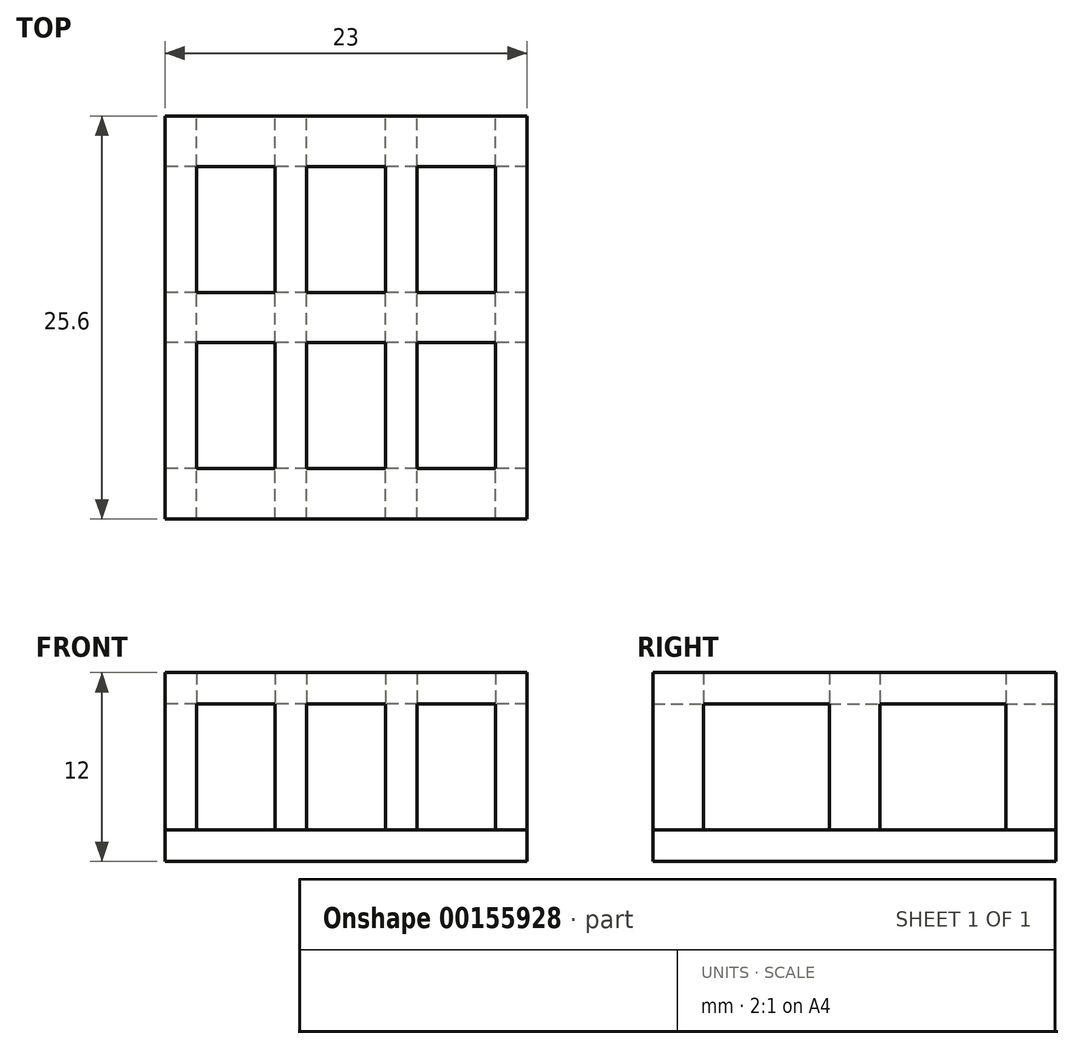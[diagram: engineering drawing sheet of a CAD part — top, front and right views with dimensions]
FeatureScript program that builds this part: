
annotation { "Feature Type Name" : "Feature", "Feature Type Description" : "" }
export const myFeature = defineFeature(function(context is Context, id is Id, definition is map)
    precondition{}
    {
        {
            var Q0;
            Q0=qCreatedBy(makeId("Top.planeOp"),FACE);
            var sketch = newSketch(context, id + "F0", { "sketchPlane" : qUnion([Q0])});
            skLineSegment(sketch, "E0", {"start": v(-38.8, 39.2) * mm, "end": v(-38.8, 40.8) * mm});
            skLineSegment(sketch, "E1", {"start": v(-33.8, 39.2) * mm, "end": v(-33.8, 40.8) * mm});
            skLineSegment(sketch, "E2", {"start": v(-31.8, 39.2) * mm, "end": v(-31.8, 40.8) * mm});
            skLineSegment(sketch, "E3", {"start": v(-26.8, 39.2) * mm, "end": v(-26.8, 40.8) * mm});
            skLineSegment(sketch, "E4", {"start": v(-24.8, 39.2) * mm, "end": v(-24.8, 40.8) * mm});
            skLineSegment(sketch, "E5", {"start": v(-19.8, 39.2) * mm, "end": v(-19.8, 40.8) * mm});
            skLineSegment(sketch, "E6", {"start": v(-17.8, 39.2) * mm, "end": v(-17.8, 40.8) * mm});
            skLineSegment(sketch, "E7.trimOffspring", {"start": v(-17.8, 40.8) * mm, "end": v(-40.8, 40.8) * mm});
            skLineSegment(sketch, "E8.trimOffspring", {"start": v(-17.8, 37.6) * mm, "end": v(-40.8, 37.6) * mm});
            skLineSegment(sketch, "E9.trimOffspring", {"start": v(-17.8, 29.6) * mm, "end": v(-40.8, 29.6) * mm});
            skLineSegment(sketch, "E10.trimOffspring", {"start": v(-17.8, 26.4) * mm, "end": v(-40.8, 26.4) * mm});
            skLineSegment(sketch, "E11.trimOffspring", {"start": v(-17.8, 18.4) * mm, "end": v(-40.8, 18.4) * mm});
            skLineSegment(sketch, "E12.trimOffspring", {"start": v(-17.8, 15.2) * mm, "end": v(-40.8, 15.2) * mm});
            skPoint(sketch, "E13.orphan", {"position": v(40.8, -40.8) * mm});
            skPoint(sketch, "E14.left.end.orphan", {"position": v(40.8, 40.8) * mm});
            skLineSegment(sketch, "E15.trimOffspring", {"start": v(-17.8, 15.2) * mm, "end": v(-17.8, 39.2) * mm});
            skLineSegment(sketch, "E16.trimOffspring", {"start": v(-19.8, 15.2) * mm, "end": v(-19.8, 39.2) * mm});
            skLineSegment(sketch, "E17.trimOffspring", {"start": v(-24.8, 15.2) * mm, "end": v(-24.8, 39.2) * mm});
            skLineSegment(sketch, "E18.trimOffspring", {"start": v(-26.8, 15.2) * mm, "end": v(-26.8, 39.2) * mm});
            skLineSegment(sketch, "E19.trimOffspring", {"start": v(-31.8, 15.2) * mm, "end": v(-31.8, 39.2) * mm});
            skLineSegment(sketch, "E20.trimOffspring", {"start": v(-33.8, 15.2) * mm, "end": v(-33.8, 39.2) * mm});
            skLineSegment(sketch, "E21.trimOffspring", {"start": v(-38.8, 15.2) * mm, "end": v(-38.8, 39.2) * mm});
            skLineSegment(sketch, "E22.trimOffspring", {"start": v(-40.8, 15.2) * mm, "end": v(-40.8, 40.8) * mm});
            skPoint(sketch, "E23.orphan", {"position": v(-4, 37.6) * mm});
            skPoint(sketch, "E24.orphan", {"position": v(-4, 29.6) * mm});
            skSolve(sketch);
        }
        {
            var Q0;
            {var subQ0=sQuery(id+"F0.wireOp",EDGE,"E20.trimOffspring");var subQ1=sQuery(id+"F0.wireOp",EDGE,"E11.trimOffspring");var subQ2=makeQuery(id+"F0.imprint","INTERSECT",VERTEX,{"derivedFrom":[subQ1,subQ0]});Q0=makeQuery(id+"F0.imprint","IMPRINT",FACE,{"disambiguationData":[TD([[makeQuery(id+"F0.imprint","IMPRINT",EDGE,{"disambiguationData":[TD([[subQ2,-1.0]])],"derivedFrom":subQ1}),1.0]])]});}
            var Q1;
            {var subQ0=sQuery(id+"F0.wireOp",EDGE,"E17.trimOffspring");var subQ1=sQuery(id+"F0.wireOp",EDGE,"E9.trimOffspring");var subQ2=makeQuery(id+"F0.imprint","INTERSECT",VERTEX,{"derivedFrom":[subQ1,subQ0]});Q1=makeQuery(id+"F0.imprint","IMPRINT",FACE,{"disambiguationData":[TD([[makeQuery(id+"F0.imprint","IMPRINT",EDGE,{"disambiguationData":[TD([[subQ2,-1.0]])],"derivedFrom":subQ1}),1.0]])]});}
            var Q2;
            {var subQ0=sQuery(id+"F0.wireOp",EDGE,"E18.trimOffspring");var subQ1=sQuery(id+"F0.wireOp",EDGE,"E8.trimOffspring");var subQ2=makeQuery(id+"F0.imprint","INTERSECT",VERTEX,{"derivedFrom":[subQ1,subQ0]});Q2=makeQuery(id+"F0.imprint","IMPRINT",FACE,{"disambiguationData":[TD([[makeQuery(id+"F0.imprint","IMPRINT",EDGE,{"disambiguationData":[TD([[subQ2,-1.0]])],"derivedFrom":subQ1}),1.0]])]});}
            var Q3;
            {var subQ0=sQuery(id+"F0.wireOp",EDGE,"E16.trimOffspring");var subQ1=sQuery(id+"F0.wireOp",EDGE,"E8.trimOffspring");var subQ2=makeQuery(id+"F0.imprint","INTERSECT",VERTEX,{"derivedFrom":[subQ1,subQ0]});Q3=makeQuery(id+"F0.imprint","IMPRINT",FACE,{"disambiguationData":[TD([[makeQuery(id+"F0.imprint","IMPRINT",EDGE,{"disambiguationData":[TD([[subQ2,-1.0]])],"derivedFrom":subQ1}),1.0]])]});}
            var Q4;
            {var subQ0=sQuery(id+"F0.wireOp",EDGE,"E20.trimOffspring");var subQ1=sQuery(id+"F0.wireOp",EDGE,"E9.trimOffspring");var subQ2=makeQuery(id+"F0.imprint","INTERSECT",VERTEX,{"derivedFrom":[subQ1,subQ0]});Q4=makeQuery(id+"F0.imprint","IMPRINT",FACE,{"disambiguationData":[TD([[makeQuery(id+"F0.imprint","IMPRINT",EDGE,{"disambiguationData":[TD([[subQ2,-1.0]])],"derivedFrom":subQ1}),1.0]])]});}
            var Q5;
            {var subQ0=sQuery(id+"F0.wireOp",EDGE,"E16.trimOffspring");var subQ1=sQuery(id+"F0.wireOp",EDGE,"E11.trimOffspring");var subQ2=makeQuery(id+"F0.imprint","INTERSECT",VERTEX,{"derivedFrom":[subQ1,subQ0]});Q5=makeQuery(id+"F0.imprint","IMPRINT",FACE,{"disambiguationData":[TD([[makeQuery(id+"F0.imprint","IMPRINT",EDGE,{"disambiguationData":[TD([[subQ2,-1.0]])],"derivedFrom":subQ1}),1.0]])]});}
            var Q6;
            {var subQ0=sQuery(id+"F0.wireOp",EDGE,"E15.trimOffspring");var subQ1=sQuery(id+"F0.wireOp",EDGE,"E10.trimOffspring");var subQ2=makeQuery(id+"F0.imprint","INTERSECT",VERTEX,{"derivedFrom":[subQ1,subQ0]});Q6=makeQuery(id+"F0.imprint","IMPRINT",FACE,{"disambiguationData":[TD([[makeQuery(id+"F0.imprint","IMPRINT",EDGE,{"disambiguationData":[TD([[subQ2,-1.0]])],"derivedFrom":subQ1}),1.0]])]});}
            var Q7;
            {var subQ0=sQuery(id+"F0.wireOp",EDGE,"E17.trimOffspring");var subQ1=sQuery(id+"F0.wireOp",EDGE,"E11.trimOffspring");var subQ2=makeQuery(id+"F0.imprint","INTERSECT",VERTEX,{"derivedFrom":[subQ1,subQ0]});Q7=makeQuery(id+"F0.imprint","IMPRINT",FACE,{"disambiguationData":[TD([[makeQuery(id+"F0.imprint","IMPRINT",EDGE,{"disambiguationData":[TD([[subQ2,-1.0]])],"derivedFrom":subQ1}),1.0]])]});}
            var Q8;
            {var subQ0=sQuery(id+"F0.wireOp",EDGE,"E22.trimOffspring");var subQ1=sQuery(id+"F0.wireOp",EDGE,"E10.trimOffspring");var subQ2=makeQuery(id+"F0.imprint","INTERSECT",VERTEX,{"derivedFrom":[subQ1,subQ0]});Q8=makeQuery(id+"F0.imprint","IMPRINT",FACE,{"disambiguationData":[TD([[makeQuery(id+"F0.imprint","IMPRINT",EDGE,{"disambiguationData":[TD([[subQ2,1.0]])],"derivedFrom":subQ1}),1.0]])]});}
            var Q9;
            {var subQ0=sQuery(id+"F0.wireOp",EDGE,"E18.trimOffspring");var subQ1=sQuery(id+"F0.wireOp",EDGE,"E10.trimOffspring");var subQ2=makeQuery(id+"F0.imprint","INTERSECT",VERTEX,{"derivedFrom":[subQ1,subQ0]});Q9=makeQuery(id+"F0.imprint","IMPRINT",FACE,{"disambiguationData":[TD([[makeQuery(id+"F0.imprint","IMPRINT",EDGE,{"disambiguationData":[TD([[subQ2,-1.0]])],"derivedFrom":subQ1}),1.0]])]});}
            var Q10;
            {var subQ0=sQuery(id+"F0.wireOp",EDGE,"E15.trimOffspring");var subQ1=sQuery(id+"F0.wireOp",EDGE,"E11.trimOffspring");var subQ2=makeQuery(id+"F0.imprint","INTERSECT",VERTEX,{"derivedFrom":[subQ1,subQ0]});Q10=makeQuery(id+"F0.imprint","IMPRINT",FACE,{"disambiguationData":[TD([[makeQuery(id+"F0.imprint","IMPRINT",EDGE,{"disambiguationData":[TD([[subQ2,-1.0]])],"derivedFrom":subQ1}),1.0]])]});}
            var Q11;
            {var subQ0=sQuery(id+"F0.wireOp",EDGE,"E22.trimOffspring");var subQ1=sQuery(id+"F0.wireOp",EDGE,"E11.trimOffspring");var subQ2=makeQuery(id+"F0.imprint","INTERSECT",VERTEX,{"derivedFrom":[subQ1,subQ0]});Q11=makeQuery(id+"F0.imprint","IMPRINT",FACE,{"disambiguationData":[TD([[makeQuery(id+"F0.imprint","IMPRINT",EDGE,{"disambiguationData":[TD([[subQ2,1.0]])],"derivedFrom":subQ1}),1.0]])]});}
            var Q12;
            {var subQ6=sQuery(id+"F0.wireOp",EDGE,"E0");Q12=makeQuery(id+"F0.imprint","IMPRINT",FACE,{"disambiguationData":[TD([[makeQuery(id+"F0.imprint","IMPRINT",EDGE,{"derivedFrom":subQ6}),-1.0]])]});}
            var Q13;
            {var subQ1=sQuery(id+"F0.wireOp",EDGE,"E2");Q13=makeQuery(id+"F0.imprint","IMPRINT",FACE,{"disambiguationData":[TD([[makeQuery(id+"F0.imprint","IMPRINT",EDGE,{"derivedFrom":subQ1}),-1.0]])]});}
            var Q14;
            {var subQ6=sQuery(id+"F0.wireOp",EDGE,"E4");Q14=makeQuery(id+"F0.imprint","IMPRINT",FACE,{"disambiguationData":[TD([[makeQuery(id+"F0.imprint","IMPRINT",EDGE,{"derivedFrom":subQ6}),-1.0]])]});}
            var Q15;
            {var subQ0=sQuery(id+"F0.wireOp",EDGE,"E15.trimOffspring");var subQ1=sQuery(id+"F0.wireOp",EDGE,"E8.trimOffspring");var subQ2=makeQuery(id+"F0.imprint","INTERSECT",VERTEX,{"derivedFrom":[subQ1,subQ0]});Q15=makeQuery(id+"F0.imprint","IMPRINT",FACE,{"disambiguationData":[TD([[makeQuery(id+"F0.imprint","IMPRINT",EDGE,{"disambiguationData":[TD([[subQ2,-1.0]])],"derivedFrom":subQ1}),1.0]])]});}
            var Q16;
            {var subQ0=sQuery(id+"F0.wireOp",EDGE,"E22.trimOffspring");var subQ1=sQuery(id+"F0.wireOp",EDGE,"E8.trimOffspring");var subQ2=makeQuery(id+"F0.imprint","INTERSECT",VERTEX,{"derivedFrom":[subQ1,subQ0]});Q16=makeQuery(id+"F0.imprint","IMPRINT",FACE,{"disambiguationData":[TD([[makeQuery(id+"F0.imprint","IMPRINT",EDGE,{"disambiguationData":[TD([[subQ2,1.0]])],"derivedFrom":subQ1}),1.0]])]});}
            var Q17;
            {var subQ0=sQuery(id+"F0.wireOp",EDGE,"E15.trimOffspring");var subQ1=sQuery(id+"F0.wireOp",EDGE,"E9.trimOffspring");var subQ2=makeQuery(id+"F0.imprint","INTERSECT",VERTEX,{"derivedFrom":[subQ1,subQ0]});Q17=makeQuery(id+"F0.imprint","IMPRINT",FACE,{"disambiguationData":[TD([[makeQuery(id+"F0.imprint","IMPRINT",EDGE,{"disambiguationData":[TD([[subQ2,-1.0]])],"derivedFrom":subQ1}),1.0]])]});}
            var Q18;
            {var subQ0=sQuery(id+"F0.wireOp",EDGE,"E22.trimOffspring");var subQ1=sQuery(id+"F0.wireOp",EDGE,"E9.trimOffspring");var subQ2=makeQuery(id+"F0.imprint","INTERSECT",VERTEX,{"derivedFrom":[subQ1,subQ0]});Q18=makeQuery(id+"F0.imprint","IMPRINT",FACE,{"disambiguationData":[TD([[makeQuery(id+"F0.imprint","IMPRINT",EDGE,{"disambiguationData":[TD([[subQ2,1.0]])],"derivedFrom":subQ1}),1.0]])]});}
            var Q19;
            {var subQ0=sQuery(id+"F0.wireOp",EDGE,"E18.trimOffspring");var subQ1=sQuery(id+"F0.wireOp",EDGE,"E9.trimOffspring");var subQ2=makeQuery(id+"F0.imprint","INTERSECT",VERTEX,{"derivedFrom":[subQ1,subQ0]});Q19=makeQuery(id+"F0.imprint","IMPRINT",FACE,{"disambiguationData":[TD([[makeQuery(id+"F0.imprint","IMPRINT",EDGE,{"disambiguationData":[TD([[subQ2,-1.0]])],"derivedFrom":subQ1}),1.0]])]});}
            var Q20;
            {var subQ0=sQuery(id+"F0.wireOp",EDGE,"E19.trimOffspring");var subQ1=sQuery(id+"F0.wireOp",EDGE,"E8.trimOffspring");var subQ2=makeQuery(id+"F0.imprint","INTERSECT",VERTEX,{"derivedFrom":[subQ1,subQ0]});Q20=makeQuery(id+"F0.imprint","IMPRINT",FACE,{"disambiguationData":[TD([[makeQuery(id+"F0.imprint","IMPRINT",EDGE,{"disambiguationData":[TD([[subQ2,-1.0]])],"derivedFrom":subQ1}),1.0]])]});}
            var Q21;
            {var subQ0=sQuery(id+"F0.wireOp",EDGE,"E17.trimOffspring");var subQ1=sQuery(id+"F0.wireOp",EDGE,"E8.trimOffspring");var subQ2=makeQuery(id+"F0.imprint","INTERSECT",VERTEX,{"derivedFrom":[subQ1,subQ0]});Q21=makeQuery(id+"F0.imprint","IMPRINT",FACE,{"disambiguationData":[TD([[makeQuery(id+"F0.imprint","IMPRINT",EDGE,{"disambiguationData":[TD([[subQ2,-1.0]])],"derivedFrom":subQ1}),1.0]])]});}
            var Q22;
            {var subQ0=sQuery(id+"F0.wireOp",EDGE,"E16.trimOffspring");var subQ1=sQuery(id+"F0.wireOp",EDGE,"E10.trimOffspring");var subQ2=makeQuery(id+"F0.imprint","INTERSECT",VERTEX,{"derivedFrom":[subQ1,subQ0]});Q22=makeQuery(id+"F0.imprint","IMPRINT",FACE,{"disambiguationData":[TD([[makeQuery(id+"F0.imprint","IMPRINT",EDGE,{"disambiguationData":[TD([[subQ2,-1.0]])],"derivedFrom":subQ1}),1.0]])]});}
            var Q23;
            {var subQ0=sQuery(id+"F0.wireOp",EDGE,"E18.trimOffspring");var subQ1=sQuery(id+"F0.wireOp",EDGE,"E11.trimOffspring");var subQ2=makeQuery(id+"F0.imprint","INTERSECT",VERTEX,{"derivedFrom":[subQ1,subQ0]});Q23=makeQuery(id+"F0.imprint","IMPRINT",FACE,{"disambiguationData":[TD([[makeQuery(id+"F0.imprint","IMPRINT",EDGE,{"disambiguationData":[TD([[subQ2,-1.0]])],"derivedFrom":subQ1}),1.0]])]});}
            var Q24;
            {var subQ0=sQuery(id+"F0.wireOp",EDGE,"E19.trimOffspring");var subQ1=sQuery(id+"F0.wireOp",EDGE,"E10.trimOffspring");var subQ2=makeQuery(id+"F0.imprint","INTERSECT",VERTEX,{"derivedFrom":[subQ1,subQ0]});Q24=makeQuery(id+"F0.imprint","IMPRINT",FACE,{"disambiguationData":[TD([[makeQuery(id+"F0.imprint","IMPRINT",EDGE,{"disambiguationData":[TD([[subQ2,-1.0]])],"derivedFrom":subQ1}),1.0]])]});}
            var Q25;
            {var subQ0=sQuery(id+"F0.wireOp",EDGE,"E19.trimOffspring");var subQ1=sQuery(id+"F0.wireOp",EDGE,"E9.trimOffspring");var subQ2=makeQuery(id+"F0.imprint","INTERSECT",VERTEX,{"derivedFrom":[subQ1,subQ0]});Q25=makeQuery(id+"F0.imprint","IMPRINT",FACE,{"disambiguationData":[TD([[makeQuery(id+"F0.imprint","IMPRINT",EDGE,{"disambiguationData":[TD([[subQ2,-1.0]])],"derivedFrom":subQ1}),1.0]])]});}
            var Q26;
            {var subQ0=sQuery(id+"F0.wireOp",EDGE,"E20.trimOffspring");var subQ1=sQuery(id+"F0.wireOp",EDGE,"E8.trimOffspring");var subQ2=makeQuery(id+"F0.imprint","INTERSECT",VERTEX,{"derivedFrom":[subQ1,subQ0]});Q26=makeQuery(id+"F0.imprint","IMPRINT",FACE,{"disambiguationData":[TD([[makeQuery(id+"F0.imprint","IMPRINT",EDGE,{"disambiguationData":[TD([[subQ2,-1.0]])],"derivedFrom":subQ1}),1.0]])]});}
            var Q27;
            {var subQ0=sQuery(id+"F0.wireOp",EDGE,"E19.trimOffspring");var subQ1=sQuery(id+"F0.wireOp",EDGE,"E11.trimOffspring");var subQ2=makeQuery(id+"F0.imprint","INTERSECT",VERTEX,{"derivedFrom":[subQ1,subQ0]});Q27=makeQuery(id+"F0.imprint","IMPRINT",FACE,{"disambiguationData":[TD([[makeQuery(id+"F0.imprint","IMPRINT",EDGE,{"disambiguationData":[TD([[subQ2,-1.0]])],"derivedFrom":subQ1}),1.0]])]});}
            var Q28;
            {var subQ0=sQuery(id+"F0.wireOp",EDGE,"E20.trimOffspring");var subQ1=sQuery(id+"F0.wireOp",EDGE,"E10.trimOffspring");var subQ2=makeQuery(id+"F0.imprint","INTERSECT",VERTEX,{"derivedFrom":[subQ1,subQ0]});Q28=makeQuery(id+"F0.imprint","IMPRINT",FACE,{"disambiguationData":[TD([[makeQuery(id+"F0.imprint","IMPRINT",EDGE,{"disambiguationData":[TD([[subQ2,-1.0]])],"derivedFrom":subQ1}),1.0]])]});}
            var Q29;
            {var subQ0=sQuery(id+"F0.wireOp",EDGE,"E17.trimOffspring");var subQ1=sQuery(id+"F0.wireOp",EDGE,"E10.trimOffspring");var subQ2=makeQuery(id+"F0.imprint","INTERSECT",VERTEX,{"derivedFrom":[subQ1,subQ0]});Q29=makeQuery(id+"F0.imprint","IMPRINT",FACE,{"disambiguationData":[TD([[makeQuery(id+"F0.imprint","IMPRINT",EDGE,{"disambiguationData":[TD([[subQ2,-1.0]])],"derivedFrom":subQ1}),1.0]])]});}
            var Q30;
            {var subQ0=sQuery(id+"F0.wireOp",EDGE,"E16.trimOffspring");var subQ1=sQuery(id+"F0.wireOp",EDGE,"E9.trimOffspring");var subQ2=makeQuery(id+"F0.imprint","INTERSECT",VERTEX,{"derivedFrom":[subQ1,subQ0]});Q30=makeQuery(id+"F0.imprint","IMPRINT",FACE,{"disambiguationData":[TD([[makeQuery(id+"F0.imprint","IMPRINT",EDGE,{"disambiguationData":[TD([[subQ2,-1.0]])],"derivedFrom":subQ1}),1.0]])]});}
            var Q31;
            {var subQ5=sQuery(id+"F0.wireOp",EDGE,"E0");Q31=makeQuery(id+"F0.imprint","IMPRINT",FACE,{"disambiguationData":[TD([[makeQuery(id+"F0.imprint","IMPRINT",EDGE,{"derivedFrom":subQ5}),1.0]])]});}
            var Q32;
            {var subQ6=sQuery(id+"F0.wireOp",EDGE,"E5");Q32=makeQuery(id+"F0.imprint","IMPRINT",FACE,{"disambiguationData":[TD([[makeQuery(id+"F0.imprint","IMPRINT",EDGE,{"derivedFrom":subQ6}),-1.0]])]});}
            var Q33;
            {var subQ1=sQuery(id+"F0.wireOp",EDGE,"E1");Q33=makeQuery(id+"F0.imprint","IMPRINT",FACE,{"disambiguationData":[TD([[makeQuery(id+"F0.imprint","IMPRINT",EDGE,{"derivedFrom":subQ1}),-1.0]])]});}
            var Q34;
            {var subQ1=sQuery(id+"F0.wireOp",EDGE,"E3");Q34=makeQuery(id+"F0.imprint","IMPRINT",FACE,{"disambiguationData":[TD([[makeQuery(id+"F0.imprint","IMPRINT",EDGE,{"derivedFrom":subQ1}),-1.0]])]});}
            extrude(context, id + "F1", {"entities" : qUnion([Q0, Q1, Q2, Q3, Q4, Q5, Q6, Q7, Q8, Q9, Q10, Q11, Q12, Q13, Q14, Q15, Q16, Q17, Q18, Q19, Q20, Q21, Q22, Q23, Q24, Q25, Q26, Q27, Q28, Q29, Q30, Q31, Q32, Q33, Q34]), "oppositeDirection" : true, "depth" : 2 * mm});
        }
        {
            var Q0;
            {var subQ5=sQuery(id+"F0.wireOp",EDGE,"E0");Q0=makeQuery(id+"F0.imprint","IMPRINT",FACE,{"disambiguationData":[TD([[makeQuery(id+"F0.imprint","IMPRINT",EDGE,{"derivedFrom":subQ5}),1.0]])]});}
            var Q1;
            {var subQ6=sQuery(id+"F0.wireOp",EDGE,"E0");Q1=makeQuery(id+"F0.imprint","IMPRINT",FACE,{"disambiguationData":[TD([[makeQuery(id+"F0.imprint","IMPRINT",EDGE,{"derivedFrom":subQ6}),-1.0]])]});}
            var Q2;
            {var subQ1=sQuery(id+"F0.wireOp",EDGE,"E2");Q2=makeQuery(id+"F0.imprint","IMPRINT",FACE,{"disambiguationData":[TD([[makeQuery(id+"F0.imprint","IMPRINT",EDGE,{"derivedFrom":subQ1}),-1.0]])]});}
            var Q3;
            {var subQ1=sQuery(id+"F0.wireOp",EDGE,"E1");Q3=makeQuery(id+"F0.imprint","IMPRINT",FACE,{"disambiguationData":[TD([[makeQuery(id+"F0.imprint","IMPRINT",EDGE,{"derivedFrom":subQ1}),-1.0]])]});}
            var Q4;
            {var subQ1=sQuery(id+"F0.wireOp",EDGE,"E3");Q4=makeQuery(id+"F0.imprint","IMPRINT",FACE,{"disambiguationData":[TD([[makeQuery(id+"F0.imprint","IMPRINT",EDGE,{"derivedFrom":subQ1}),-1.0]])]});}
            var Q5;
            {var subQ6=sQuery(id+"F0.wireOp",EDGE,"E4");Q5=makeQuery(id+"F0.imprint","IMPRINT",FACE,{"disambiguationData":[TD([[makeQuery(id+"F0.imprint","IMPRINT",EDGE,{"derivedFrom":subQ6}),-1.0]])]});}
            var Q6;
            {var subQ6=sQuery(id+"F0.wireOp",EDGE,"E5");Q6=makeQuery(id+"F0.imprint","IMPRINT",FACE,{"disambiguationData":[TD([[makeQuery(id+"F0.imprint","IMPRINT",EDGE,{"derivedFrom":subQ6}),-1.0]])]});}
            var Q7;
            {var subQ0=sQuery(id+"F0.wireOp",EDGE,"E15.trimOffspring");var subQ1=sQuery(id+"F0.wireOp",EDGE,"E8.trimOffspring");var subQ2=makeQuery(id+"F0.imprint","INTERSECT",VERTEX,{"derivedFrom":[subQ1,subQ0]});Q7=makeQuery(id+"F0.imprint","IMPRINT",FACE,{"disambiguationData":[TD([[makeQuery(id+"F0.imprint","IMPRINT",EDGE,{"disambiguationData":[TD([[subQ2,-1.0]])],"derivedFrom":subQ1}),1.0]])]});}
            var Q8;
            {var subQ0=sQuery(id+"F0.wireOp",EDGE,"E15.trimOffspring");var subQ1=sQuery(id+"F0.wireOp",EDGE,"E9.trimOffspring");var subQ2=makeQuery(id+"F0.imprint","INTERSECT",VERTEX,{"derivedFrom":[subQ1,subQ0]});Q8=makeQuery(id+"F0.imprint","IMPRINT",FACE,{"disambiguationData":[TD([[makeQuery(id+"F0.imprint","IMPRINT",EDGE,{"disambiguationData":[TD([[subQ2,-1.0]])],"derivedFrom":subQ1}),1.0]])]});}
            var Q9;
            {var subQ0=sQuery(id+"F0.wireOp",EDGE,"E15.trimOffspring");var subQ1=sQuery(id+"F0.wireOp",EDGE,"E10.trimOffspring");var subQ2=makeQuery(id+"F0.imprint","INTERSECT",VERTEX,{"derivedFrom":[subQ1,subQ0]});Q9=makeQuery(id+"F0.imprint","IMPRINT",FACE,{"disambiguationData":[TD([[makeQuery(id+"F0.imprint","IMPRINT",EDGE,{"disambiguationData":[TD([[subQ2,-1.0]])],"derivedFrom":subQ1}),1.0]])]});}
            var Q10;
            {var subQ0=sQuery(id+"F0.wireOp",EDGE,"E15.trimOffspring");var subQ1=sQuery(id+"F0.wireOp",EDGE,"E11.trimOffspring");var subQ2=makeQuery(id+"F0.imprint","INTERSECT",VERTEX,{"derivedFrom":[subQ1,subQ0]});Q10=makeQuery(id+"F0.imprint","IMPRINT",FACE,{"disambiguationData":[TD([[makeQuery(id+"F0.imprint","IMPRINT",EDGE,{"disambiguationData":[TD([[subQ2,-1.0]])],"derivedFrom":subQ1}),1.0]])]});}
            var Q11;
            {var subQ0=sQuery(id+"F0.wireOp",EDGE,"E16.trimOffspring");var subQ1=sQuery(id+"F0.wireOp",EDGE,"E11.trimOffspring");var subQ2=makeQuery(id+"F0.imprint","INTERSECT",VERTEX,{"derivedFrom":[subQ1,subQ0]});Q11=makeQuery(id+"F0.imprint","IMPRINT",FACE,{"disambiguationData":[TD([[makeQuery(id+"F0.imprint","IMPRINT",EDGE,{"disambiguationData":[TD([[subQ2,-1.0]])],"derivedFrom":subQ1}),1.0]])]});}
            var Q12;
            {var subQ0=sQuery(id+"F0.wireOp",EDGE,"E17.trimOffspring");var subQ1=sQuery(id+"F0.wireOp",EDGE,"E11.trimOffspring");var subQ2=makeQuery(id+"F0.imprint","INTERSECT",VERTEX,{"derivedFrom":[subQ1,subQ0]});Q12=makeQuery(id+"F0.imprint","IMPRINT",FACE,{"disambiguationData":[TD([[makeQuery(id+"F0.imprint","IMPRINT",EDGE,{"disambiguationData":[TD([[subQ2,-1.0]])],"derivedFrom":subQ1}),1.0]])]});}
            var Q13;
            {var subQ0=sQuery(id+"F0.wireOp",EDGE,"E18.trimOffspring");var subQ1=sQuery(id+"F0.wireOp",EDGE,"E11.trimOffspring");var subQ2=makeQuery(id+"F0.imprint","INTERSECT",VERTEX,{"derivedFrom":[subQ1,subQ0]});Q13=makeQuery(id+"F0.imprint","IMPRINT",FACE,{"disambiguationData":[TD([[makeQuery(id+"F0.imprint","IMPRINT",EDGE,{"disambiguationData":[TD([[subQ2,-1.0]])],"derivedFrom":subQ1}),1.0]])]});}
            var Q14;
            {var subQ0=sQuery(id+"F0.wireOp",EDGE,"E19.trimOffspring");var subQ1=sQuery(id+"F0.wireOp",EDGE,"E11.trimOffspring");var subQ2=makeQuery(id+"F0.imprint","INTERSECT",VERTEX,{"derivedFrom":[subQ1,subQ0]});Q14=makeQuery(id+"F0.imprint","IMPRINT",FACE,{"disambiguationData":[TD([[makeQuery(id+"F0.imprint","IMPRINT",EDGE,{"disambiguationData":[TD([[subQ2,-1.0]])],"derivedFrom":subQ1}),1.0]])]});}
            var Q15;
            {var subQ0=sQuery(id+"F0.wireOp",EDGE,"E20.trimOffspring");var subQ1=sQuery(id+"F0.wireOp",EDGE,"E11.trimOffspring");var subQ2=makeQuery(id+"F0.imprint","INTERSECT",VERTEX,{"derivedFrom":[subQ1,subQ0]});Q15=makeQuery(id+"F0.imprint","IMPRINT",FACE,{"disambiguationData":[TD([[makeQuery(id+"F0.imprint","IMPRINT",EDGE,{"disambiguationData":[TD([[subQ2,-1.0]])],"derivedFrom":subQ1}),1.0]])]});}
            var Q16;
            {var subQ0=sQuery(id+"F0.wireOp",EDGE,"E22.trimOffspring");var subQ1=sQuery(id+"F0.wireOp",EDGE,"E11.trimOffspring");var subQ2=makeQuery(id+"F0.imprint","INTERSECT",VERTEX,{"derivedFrom":[subQ1,subQ0]});Q16=makeQuery(id+"F0.imprint","IMPRINT",FACE,{"disambiguationData":[TD([[makeQuery(id+"F0.imprint","IMPRINT",EDGE,{"disambiguationData":[TD([[subQ2,1.0]])],"derivedFrom":subQ1}),1.0]])]});}
            var Q17;
            {var subQ0=sQuery(id+"F0.wireOp",EDGE,"E22.trimOffspring");var subQ1=sQuery(id+"F0.wireOp",EDGE,"E10.trimOffspring");var subQ2=makeQuery(id+"F0.imprint","INTERSECT",VERTEX,{"derivedFrom":[subQ1,subQ0]});Q17=makeQuery(id+"F0.imprint","IMPRINT",FACE,{"disambiguationData":[TD([[makeQuery(id+"F0.imprint","IMPRINT",EDGE,{"disambiguationData":[TD([[subQ2,1.0]])],"derivedFrom":subQ1}),1.0]])]});}
            var Q18;
            {var subQ0=sQuery(id+"F0.wireOp",EDGE,"E22.trimOffspring");var subQ1=sQuery(id+"F0.wireOp",EDGE,"E9.trimOffspring");var subQ2=makeQuery(id+"F0.imprint","INTERSECT",VERTEX,{"derivedFrom":[subQ1,subQ0]});Q18=makeQuery(id+"F0.imprint","IMPRINT",FACE,{"disambiguationData":[TD([[makeQuery(id+"F0.imprint","IMPRINT",EDGE,{"disambiguationData":[TD([[subQ2,1.0]])],"derivedFrom":subQ1}),1.0]])]});}
            var Q19;
            {var subQ0=sQuery(id+"F0.wireOp",EDGE,"E22.trimOffspring");var subQ1=sQuery(id+"F0.wireOp",EDGE,"E8.trimOffspring");var subQ2=makeQuery(id+"F0.imprint","INTERSECT",VERTEX,{"derivedFrom":[subQ1,subQ0]});Q19=makeQuery(id+"F0.imprint","IMPRINT",FACE,{"disambiguationData":[TD([[makeQuery(id+"F0.imprint","IMPRINT",EDGE,{"disambiguationData":[TD([[subQ2,1.0]])],"derivedFrom":subQ1}),1.0]])]});}
            var Q20;
            {var subQ0=sQuery(id+"F0.wireOp",EDGE,"E20.trimOffspring");var subQ1=sQuery(id+"F0.wireOp",EDGE,"E9.trimOffspring");var subQ2=makeQuery(id+"F0.imprint","INTERSECT",VERTEX,{"derivedFrom":[subQ1,subQ0]});Q20=makeQuery(id+"F0.imprint","IMPRINT",FACE,{"disambiguationData":[TD([[makeQuery(id+"F0.imprint","IMPRINT",EDGE,{"disambiguationData":[TD([[subQ2,-1.0]])],"derivedFrom":subQ1}),1.0]])]});}
            var Q21;
            {var subQ0=sQuery(id+"F0.wireOp",EDGE,"E19.trimOffspring");var subQ1=sQuery(id+"F0.wireOp",EDGE,"E9.trimOffspring");var subQ2=makeQuery(id+"F0.imprint","INTERSECT",VERTEX,{"derivedFrom":[subQ1,subQ0]});Q21=makeQuery(id+"F0.imprint","IMPRINT",FACE,{"disambiguationData":[TD([[makeQuery(id+"F0.imprint","IMPRINT",EDGE,{"disambiguationData":[TD([[subQ2,-1.0]])],"derivedFrom":subQ1}),1.0]])]});}
            var Q22;
            {var subQ0=sQuery(id+"F0.wireOp",EDGE,"E19.trimOffspring");var subQ1=sQuery(id+"F0.wireOp",EDGE,"E8.trimOffspring");var subQ2=makeQuery(id+"F0.imprint","INTERSECT",VERTEX,{"derivedFrom":[subQ1,subQ0]});Q22=makeQuery(id+"F0.imprint","IMPRINT",FACE,{"disambiguationData":[TD([[makeQuery(id+"F0.imprint","IMPRINT",EDGE,{"disambiguationData":[TD([[subQ2,-1.0]])],"derivedFrom":subQ1}),1.0]])]});}
            var Q23;
            {var subQ0=sQuery(id+"F0.wireOp",EDGE,"E19.trimOffspring");var subQ1=sQuery(id+"F0.wireOp",EDGE,"E10.trimOffspring");var subQ2=makeQuery(id+"F0.imprint","INTERSECT",VERTEX,{"derivedFrom":[subQ1,subQ0]});Q23=makeQuery(id+"F0.imprint","IMPRINT",FACE,{"disambiguationData":[TD([[makeQuery(id+"F0.imprint","IMPRINT",EDGE,{"disambiguationData":[TD([[subQ2,-1.0]])],"derivedFrom":subQ1}),1.0]])]});}
            var Q24;
            {var subQ0=sQuery(id+"F0.wireOp",EDGE,"E18.trimOffspring");var subQ1=sQuery(id+"F0.wireOp",EDGE,"E9.trimOffspring");var subQ2=makeQuery(id+"F0.imprint","INTERSECT",VERTEX,{"derivedFrom":[subQ1,subQ0]});Q24=makeQuery(id+"F0.imprint","IMPRINT",FACE,{"disambiguationData":[TD([[makeQuery(id+"F0.imprint","IMPRINT",EDGE,{"disambiguationData":[TD([[subQ2,-1.0]])],"derivedFrom":subQ1}),1.0]])]});}
            var Q25;
            {var subQ0=sQuery(id+"F0.wireOp",EDGE,"E16.trimOffspring");var subQ1=sQuery(id+"F0.wireOp",EDGE,"E9.trimOffspring");var subQ2=makeQuery(id+"F0.imprint","INTERSECT",VERTEX,{"derivedFrom":[subQ1,subQ0]});Q25=makeQuery(id+"F0.imprint","IMPRINT",FACE,{"disambiguationData":[TD([[makeQuery(id+"F0.imprint","IMPRINT",EDGE,{"disambiguationData":[TD([[subQ2,-1.0]])],"derivedFrom":subQ1}),1.0]])]});}
            var Q26;
            {var subQ0=sQuery(id+"F0.wireOp",EDGE,"E17.trimOffspring");var subQ1=sQuery(id+"F0.wireOp",EDGE,"E9.trimOffspring");var subQ2=makeQuery(id+"F0.imprint","INTERSECT",VERTEX,{"derivedFrom":[subQ1,subQ0]});Q26=makeQuery(id+"F0.imprint","IMPRINT",FACE,{"disambiguationData":[TD([[makeQuery(id+"F0.imprint","IMPRINT",EDGE,{"disambiguationData":[TD([[subQ2,-1.0]])],"derivedFrom":subQ1}),1.0]])]});}
            var Q27;
            {var subQ0=sQuery(id+"F0.wireOp",EDGE,"E17.trimOffspring");var subQ1=sQuery(id+"F0.wireOp",EDGE,"E8.trimOffspring");var subQ2=makeQuery(id+"F0.imprint","INTERSECT",VERTEX,{"derivedFrom":[subQ1,subQ0]});Q27=makeQuery(id+"F0.imprint","IMPRINT",FACE,{"disambiguationData":[TD([[makeQuery(id+"F0.imprint","IMPRINT",EDGE,{"disambiguationData":[TD([[subQ2,-1.0]])],"derivedFrom":subQ1}),1.0]])]});}
            var Q28;
            {var subQ0=sQuery(id+"F0.wireOp",EDGE,"E17.trimOffspring");var subQ1=sQuery(id+"F0.wireOp",EDGE,"E10.trimOffspring");var subQ2=makeQuery(id+"F0.imprint","INTERSECT",VERTEX,{"derivedFrom":[subQ1,subQ0]});Q28=makeQuery(id+"F0.imprint","IMPRINT",FACE,{"disambiguationData":[TD([[makeQuery(id+"F0.imprint","IMPRINT",EDGE,{"disambiguationData":[TD([[subQ2,-1.0]])],"derivedFrom":subQ1}),1.0]])]});}
            extrude(context, id + "F2", {"entities" : qUnion([Q0, Q1, Q2, Q3, Q4, Q5, Q6, Q7, Q8, Q9, Q10, Q11, Q12, Q13, Q14, Q15, Q16, Q17, Q18, Q19, Q20, Q21, Q22, Q23, Q24, Q25, Q26, Q27, Q28]), "depth" : 10 * mm});
        }
        {
            var Q0;
            {var subQ0=sQuery(id+"F0.wireOp",EDGE,"E22.trimOffspring");var subQ1=sQuery(id+"F0.wireOp",EDGE,"E8.trimOffspring");var subQ2=makeQuery(id+"F0.imprint","INTERSECT",VERTEX,{"derivedFrom":[subQ1,subQ0]});Q0=makeQuery(id+"F0.imprint","IMPRINT",FACE,{"disambiguationData":[TD([[makeQuery(id+"F0.imprint","IMPRINT",EDGE,{"disambiguationData":[TD([[subQ2,1.0]])],"derivedFrom":subQ1}),1.0]])]});}
            var Q1;
            {var subQ6=sQuery(id+"F0.wireOp",EDGE,"E0");Q1=makeQuery(id+"F0.imprint","IMPRINT",FACE,{"disambiguationData":[TD([[makeQuery(id+"F0.imprint","IMPRINT",EDGE,{"derivedFrom":subQ6}),-1.0]])]});}
            var Q2;
            {var subQ1=sQuery(id+"F0.wireOp",EDGE,"E2");Q2=makeQuery(id+"F0.imprint","IMPRINT",FACE,{"disambiguationData":[TD([[makeQuery(id+"F0.imprint","IMPRINT",EDGE,{"derivedFrom":subQ1}),-1.0]])]});}
            var Q3;
            {var subQ6=sQuery(id+"F0.wireOp",EDGE,"E4");Q3=makeQuery(id+"F0.imprint","IMPRINT",FACE,{"disambiguationData":[TD([[makeQuery(id+"F0.imprint","IMPRINT",EDGE,{"derivedFrom":subQ6}),-1.0]])]});}
            var Q4;
            {var subQ0=sQuery(id+"F0.wireOp",EDGE,"E15.trimOffspring");var subQ1=sQuery(id+"F0.wireOp",EDGE,"E8.trimOffspring");var subQ2=makeQuery(id+"F0.imprint","INTERSECT",VERTEX,{"derivedFrom":[subQ1,subQ0]});Q4=makeQuery(id+"F0.imprint","IMPRINT",FACE,{"disambiguationData":[TD([[makeQuery(id+"F0.imprint","IMPRINT",EDGE,{"disambiguationData":[TD([[subQ2,-1.0]])],"derivedFrom":subQ1}),1.0]])]});}
            var Q5;
            {var subQ0=sQuery(id+"F0.wireOp",EDGE,"E15.trimOffspring");var subQ1=sQuery(id+"F0.wireOp",EDGE,"E10.trimOffspring");var subQ2=makeQuery(id+"F0.imprint","INTERSECT",VERTEX,{"derivedFrom":[subQ1,subQ0]});Q5=makeQuery(id+"F0.imprint","IMPRINT",FACE,{"disambiguationData":[TD([[makeQuery(id+"F0.imprint","IMPRINT",EDGE,{"disambiguationData":[TD([[subQ2,-1.0]])],"derivedFrom":subQ1}),1.0]])]});}
            var Q6;
            {var subQ0=sQuery(id+"F0.wireOp",EDGE,"E17.trimOffspring");var subQ1=sQuery(id+"F0.wireOp",EDGE,"E10.trimOffspring");var subQ2=makeQuery(id+"F0.imprint","INTERSECT",VERTEX,{"derivedFrom":[subQ1,subQ0]});Q6=makeQuery(id+"F0.imprint","IMPRINT",FACE,{"disambiguationData":[TD([[makeQuery(id+"F0.imprint","IMPRINT",EDGE,{"disambiguationData":[TD([[subQ2,-1.0]])],"derivedFrom":subQ1}),1.0]])]});}
            var Q7;
            {var subQ0=sQuery(id+"F0.wireOp",EDGE,"E19.trimOffspring");var subQ1=sQuery(id+"F0.wireOp",EDGE,"E10.trimOffspring");var subQ2=makeQuery(id+"F0.imprint","INTERSECT",VERTEX,{"derivedFrom":[subQ1,subQ0]});Q7=makeQuery(id+"F0.imprint","IMPRINT",FACE,{"disambiguationData":[TD([[makeQuery(id+"F0.imprint","IMPRINT",EDGE,{"disambiguationData":[TD([[subQ2,-1.0]])],"derivedFrom":subQ1}),1.0]])]});}
            var Q8;
            {var subQ0=sQuery(id+"F0.wireOp",EDGE,"E22.trimOffspring");var subQ1=sQuery(id+"F0.wireOp",EDGE,"E10.trimOffspring");var subQ2=makeQuery(id+"F0.imprint","INTERSECT",VERTEX,{"derivedFrom":[subQ1,subQ0]});Q8=makeQuery(id+"F0.imprint","IMPRINT",FACE,{"disambiguationData":[TD([[makeQuery(id+"F0.imprint","IMPRINT",EDGE,{"disambiguationData":[TD([[subQ2,1.0]])],"derivedFrom":subQ1}),1.0]])]});}
            var Q9;
            {var subQ0=sQuery(id+"F0.wireOp",EDGE,"E20.trimOffspring");var subQ1=sQuery(id+"F0.wireOp",EDGE,"E11.trimOffspring");var subQ2=makeQuery(id+"F0.imprint","INTERSECT",VERTEX,{"derivedFrom":[subQ1,subQ0]});Q9=makeQuery(id+"F0.imprint","IMPRINT",FACE,{"disambiguationData":[TD([[makeQuery(id+"F0.imprint","IMPRINT",EDGE,{"disambiguationData":[TD([[subQ2,-1.0]])],"derivedFrom":subQ1}),1.0]])]});}
            var Q10;
            {var subQ0=sQuery(id+"F0.wireOp",EDGE,"E18.trimOffspring");var subQ1=sQuery(id+"F0.wireOp",EDGE,"E11.trimOffspring");var subQ2=makeQuery(id+"F0.imprint","INTERSECT",VERTEX,{"derivedFrom":[subQ1,subQ0]});Q10=makeQuery(id+"F0.imprint","IMPRINT",FACE,{"disambiguationData":[TD([[makeQuery(id+"F0.imprint","IMPRINT",EDGE,{"disambiguationData":[TD([[subQ2,-1.0]])],"derivedFrom":subQ1}),1.0]])]});}
            var Q11;
            {var subQ0=sQuery(id+"F0.wireOp",EDGE,"E16.trimOffspring");var subQ1=sQuery(id+"F0.wireOp",EDGE,"E11.trimOffspring");var subQ2=makeQuery(id+"F0.imprint","INTERSECT",VERTEX,{"derivedFrom":[subQ1,subQ0]});Q11=makeQuery(id+"F0.imprint","IMPRINT",FACE,{"disambiguationData":[TD([[makeQuery(id+"F0.imprint","IMPRINT",EDGE,{"disambiguationData":[TD([[subQ2,-1.0]])],"derivedFrom":subQ1}),1.0]])]});}
            var Q12;
            {var subQ0=sQuery(id+"F0.wireOp",EDGE,"E16.trimOffspring");var subQ1=sQuery(id+"F0.wireOp",EDGE,"E9.trimOffspring");var subQ2=makeQuery(id+"F0.imprint","INTERSECT",VERTEX,{"derivedFrom":[subQ1,subQ0]});Q12=makeQuery(id+"F0.imprint","IMPRINT",FACE,{"disambiguationData":[TD([[makeQuery(id+"F0.imprint","IMPRINT",EDGE,{"disambiguationData":[TD([[subQ2,-1.0]])],"derivedFrom":subQ1}),1.0]])]});}
            var Q13;
            {var subQ0=sQuery(id+"F0.wireOp",EDGE,"E18.trimOffspring");var subQ1=sQuery(id+"F0.wireOp",EDGE,"E9.trimOffspring");var subQ2=makeQuery(id+"F0.imprint","INTERSECT",VERTEX,{"derivedFrom":[subQ1,subQ0]});Q13=makeQuery(id+"F0.imprint","IMPRINT",FACE,{"disambiguationData":[TD([[makeQuery(id+"F0.imprint","IMPRINT",EDGE,{"disambiguationData":[TD([[subQ2,-1.0]])],"derivedFrom":subQ1}),1.0]])]});}
            var Q14;
            {var subQ0=sQuery(id+"F0.wireOp",EDGE,"E20.trimOffspring");var subQ1=sQuery(id+"F0.wireOp",EDGE,"E9.trimOffspring");var subQ2=makeQuery(id+"F0.imprint","INTERSECT",VERTEX,{"derivedFrom":[subQ1,subQ0]});Q14=makeQuery(id+"F0.imprint","IMPRINT",FACE,{"disambiguationData":[TD([[makeQuery(id+"F0.imprint","IMPRINT",EDGE,{"disambiguationData":[TD([[subQ2,-1.0]])],"derivedFrom":subQ1}),1.0]])]});}
            var Q15;
            {var subQ0=sQuery(id+"F0.wireOp",EDGE,"E19.trimOffspring");var subQ1=sQuery(id+"F0.wireOp",EDGE,"E8.trimOffspring");var subQ2=makeQuery(id+"F0.imprint","INTERSECT",VERTEX,{"derivedFrom":[subQ1,subQ0]});Q15=makeQuery(id+"F0.imprint","IMPRINT",FACE,{"disambiguationData":[TD([[makeQuery(id+"F0.imprint","IMPRINT",EDGE,{"disambiguationData":[TD([[subQ2,-1.0]])],"derivedFrom":subQ1}),1.0]])]});}
            var Q16;
            {var subQ0=sQuery(id+"F0.wireOp",EDGE,"E17.trimOffspring");var subQ1=sQuery(id+"F0.wireOp",EDGE,"E8.trimOffspring");var subQ2=makeQuery(id+"F0.imprint","INTERSECT",VERTEX,{"derivedFrom":[subQ1,subQ0]});Q16=makeQuery(id+"F0.imprint","IMPRINT",FACE,{"disambiguationData":[TD([[makeQuery(id+"F0.imprint","IMPRINT",EDGE,{"disambiguationData":[TD([[subQ2,-1.0]])],"derivedFrom":subQ1}),1.0]])]});}
            extrude(context, id + "F3", {"entities" : qUnion([Q0, Q1, Q2, Q3, Q4, Q5, Q6, Q7, Q8, Q9, Q10, Q11, Q12, Q13, Q14, Q15, Q16]), "operationType" : NewBodyOperationType.REMOVE, "depth" : 8 * mm});
        }
    });
